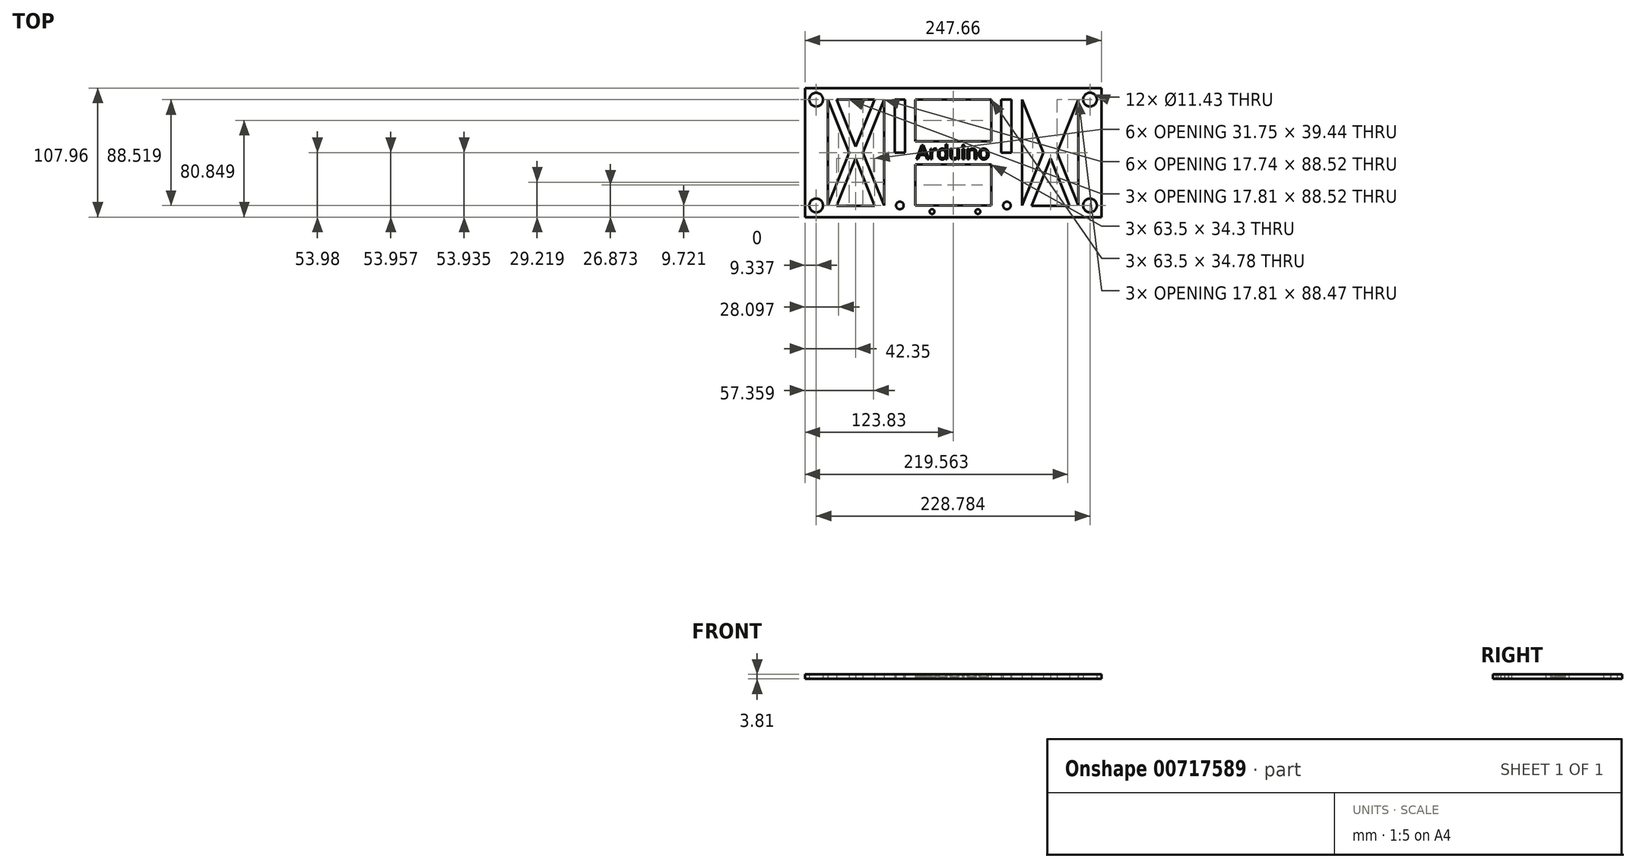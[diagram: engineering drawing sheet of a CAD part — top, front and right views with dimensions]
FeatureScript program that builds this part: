
annotation { "Feature Type Name" : "Feature", "Feature Type Description" : "" }
export const myFeature = defineFeature(function(context is Context, id is Id, definition is map)
    precondition{}
    {
        {
            var Q0;
            Q0=qCreatedBy(makeId("Top.planeOp"),FACE);
            var sketch = newSketch(context, id + "F0", { "sketchPlane" : qUnion([Q0])});
            skLineSegment(sketch, "E0.bottom", {"start": v(-123.83, 53.97) * mm, "end": v(123.83, 53.97) * mm});
            skLineSegment(sketch, "E0.top", {"start": v(-123.83, -53.97) * mm, "end": v(123.83, -53.97) * mm});
            skLineSegment(sketch, "E0.left", {"start": v(-123.83, 53.97) * mm, "end": v(-123.83, -53.97) * mm});
            skLineSegment(sketch, "E0.right", {"start": v(123.83, 53.97) * mm, "end": v(123.83, -53.97) * mm});
            skPoint(sketch, "E0.middle", {"position": v(0, 0) * mm});
            skLineSegment(sketch, "E1.bottom", {"start": v(-31.75, 44.26) * mm, "end": v(31.75, 44.26) * mm});
            skLineSegment(sketch, "E1.top", {"start": v(-31.75, -44.26) * mm, "end": v(31.75, -44.26) * mm});
            skLineSegment(sketch, "E1.left", {"start": v(-31.75, 44.26) * mm, "end": v(-31.75, 9.48) * mm});
            skLineSegment(sketch, "E1.right", {"start": v(31.75, 44.26) * mm, "end": v(31.75, 9.48) * mm});
            skLineSegment(sketch, "E2", {"start": v(-104.64, 44.26) * mm, "end": v(-104.64, -44.26) * mm});
            skLineSegment(sketch, "E3.2.0.0", {"start": v(-57.6, 44.21) * mm, "end": v(-57.6, -44.3) * mm});
            skLineSegment(sketch, "E4", {"start": v(-65.6, 44.21) * mm, "end": v(-97.36, 44.26) * mm});
            skLineSegment(sketch, "E5", {"start": v(-97.36, -44.48) * mm, "end": v(-65.6, -44.48) * mm});
            skLineSegment(sketch, "E6.bottom", {"start": v(-48.82, 44.21) * mm, "end": v(-40.12, 44.21) * mm});
            skLineSegment(sketch, "E6.top", {"start": v(-48.82, 0) * mm, "end": v(-40.12, 0) * mm});
            skLineSegment(sketch, "E6.left", {"start": v(-48.82, 44.21) * mm, "end": v(-48.82, 0) * mm});
            skLineSegment(sketch, "E6.right", {"start": v(-40.12, 44.21) * mm, "end": v(-40.12, 0) * mm});
            skLineSegment(sketch, "E7.1.0.0", {"start": v(97.36, 44.45) * mm, "end": v(65.6, 44.45) * mm});
            skLineSegment(sketch, "E7.1.0.5", {"start": v(65.6, -44.48) * mm, "end": v(97.36, -44.48) * mm});
            skLineSegment(sketch, "E7.1.0.8", {"start": v(104.62, 44.45) * mm, "end": v(104.64, -44.45) * mm});
            skLineSegment(sketch, "E7.1.0.9", {"start": v(57.6, 44.45) * mm, "end": v(57.6, -44.45) * mm});
            skLineSegment(sketch, "E8", {"start": v(0, 0) * mm, "end": v(0, 1.06) * mm, "construction": true});
            skLineSegment(sketch, "E9", {"start": v(0, 6.02) * mm, "end": v(0, 0) * mm, "construction": true});
            skLineSegment(sketch, "E10", {"start": v(0, 0) * mm, "end": v(0, -6.02) * mm, "construction": true});
            skPoint(sketch, "E11.endSnap0", {"position": v(-57.6, -0.04) * mm});
            skLineSegment(sketch, "E12", {"start": v(-75.34, -0.04) * mm, "end": v(-57.6, -44.3) * mm});
            skLineSegment(sketch, "E13", {"start": v(-86.83, 0) * mm, "end": v(-104.64, -44.26) * mm});
            skLineSegment(sketch, "E14", {"start": v(-97.36, -44.48) * mm, "end": v(-81.48, -5.04) * mm});
            skLineSegment(sketch, "E15", {"start": v(-81.48, -5.04) * mm, "end": v(-65.6, -44.48) * mm});
            skLineSegment(sketch, "E16", {"start": v(-57.6, 44.21) * mm, "end": v(-75.34, -0.04) * mm});
            skLineSegment(sketch, "E17", {"start": v(-104.64, 44.26) * mm, "end": v(-86.83, 0) * mm});
            skLineSegment(sketch, "E18", {"start": v(-97.36, 44.26) * mm, "end": v(-81.54, 4.8) * mm});
            skLineSegment(sketch, "E19", {"start": v(-81.54, 4.8) * mm, "end": v(-65.6, 44.21) * mm});
            skLineSegment(sketch, "E20.MirrorCS", {"start": v(81.54, 4.8) * mm, "end": v(65.6, 44.21) * mm});
            skLineSegment(sketch, "E21.MirrorCS", {"start": v(97.36, 44.26) * mm, "end": v(81.54, 4.8) * mm});
            skLineSegment(sketch, "E22.MirrorCS", {"start": v(104.64, 44.26) * mm, "end": v(86.83, 0) * mm});
            skLineSegment(sketch, "E23.MirrorCS", {"start": v(57.6, 44.21) * mm, "end": v(75.34, -0.04) * mm});
            skLineSegment(sketch, "E24.MirrorCS", {"start": v(75.34, -0.04) * mm, "end": v(57.6, -44.3) * mm});
            skLineSegment(sketch, "E25.MirrorCS", {"start": v(81.48, -5.04) * mm, "end": v(65.6, -44.48) * mm});
            skLineSegment(sketch, "E26.MirrorCS", {"start": v(97.36, -44.48) * mm, "end": v(81.48, -5.04) * mm});
            skLineSegment(sketch, "E27.MirrorCS", {"start": v(86.83, 0) * mm, "end": v(104.64, -44.26) * mm});
            skLineSegment(sketch, "E28", {"start": v(-31.75, 9.48) * mm, "end": v(31.75, 9.48) * mm});
            skLineSegment(sketch, "E29", {"start": v(-31.75, -9.95) * mm, "end": v(31.75, -9.95) * mm});
            skLineSegment(sketch, "E30.trimOffspring", {"start": v(-31.75, -9.95) * mm, "end": v(-31.75, -44.26) * mm});
            skLineSegment(sketch, "E31.trimOffspring", {"start": v(31.75, -9.95) * mm, "end": v(31.75, -44.26) * mm});
            skCircle(sketch, "E32", {"center": v(-114.5, -44.26) * mm, "radius": 5.72 * mm});
            skCircle(sketch, "E33", {"center": v(-114.5, 44.26) * mm, "radius": 5.72 * mm});
            skCircle(sketch, "E34", {"center": v(114.3, 44.26) * mm, "radius": 5.72 * mm});
            skCircle(sketch, "E35", {"center": v(114.3, -44.26) * mm, "radius": 5.72 * mm});
            skLineSegment(sketch, "E36", {"start": v(40.03, 44.26) * mm, "end": v(40.03, 0) * mm});
            skLineSegment(sketch, "E37", {"start": v(40.03, 0) * mm, "end": v(48.72, 0) * mm});
            skLineSegment(sketch, "E38", {"start": v(48.72, 0) * mm, "end": v(48.72, 44.45) * mm});
            skLineSegment(sketch, "E39", {"start": v(48.72, 44.45) * mm, "end": v(40.03, 44.26) * mm});
            skCircle(sketch, "E40", {"center": v(-44.53, -44.26) * mm, "radius": 3.18 * mm});
            skCircle(sketch, "E41", {"center": v(44.87, -44.3) * mm, "radius": 3.18 * mm});
            skCircle(sketch, "E42", {"center": v(-17.66, -49.42) * mm, "radius": 2.03 * mm});
            skCircle(sketch, "E43", {"center": v(20.65, -49.42) * mm, "radius": 2.03 * mm});
            skSolve(sketch);
        }
        {
            var Q0;
            Q0=makeQuery(id+"F0.imprint","IMPRINT",FACE,{"disambiguationData":[TD([[makeQuery(id+"F0.imprint","IMPRINT",EDGE,{"derivedFrom":sQuery(id+"F0.wireOp",EDGE,"E0.bottom")}),-1.0]])]});
            extrude(context, id + "F1", {"entities" : qUnion([Q0]), "depth" : 3.8 * mm, "offsetDistance" : 25.4 * mm});
        }
        {
            var Q0;
            Q0=makeQuery(id+"F1.opExtrude","CAP_FACE",FACE,{"disambiguationData":[OSD([sQuery(id+"F0.wireOp",EDGE,"E0.bottom"),sQuery(id+"F0.wireOp",EDGE,"E0.top"),sQuery(id+"F0.wireOp",EDGE,"E0.left"),sQuery(id+"F0.wireOp",EDGE,"E0.right"),sQuery(id+"F0.wireOp",EDGE,"E1.bottom"),sQuery(id+"F0.wireOp",EDGE,"E1.top"),sQuery(id+"F0.wireOp",EDGE,"E1.left"),sQuery(id+"F0.wireOp",EDGE,"E1.right"),sQuery(id+"F0.wireOp",EDGE,"E2"),sQuery(id+"F0.wireOp",EDGE,"E3.2.0.0"),sQuery(id+"F0.wireOp",EDGE,"E4"),sQuery(id+"F0.wireOp",EDGE,"E5"),sQuery(id+"F0.wireOp",EDGE,"E6.bottom"),sQuery(id+"F0.wireOp",EDGE,"E6.top"),sQuery(id+"F0.wireOp",EDGE,"E6.left"),sQuery(id+"F0.wireOp",EDGE,"E6.right"),sQuery(id+"F0.wireOp",EDGE,"EDbcc8To-gHE8-0e38-XdKg-VJ03WfKCGKzv.top"),sQuery(id+"F0.wireOp",EDGE,"PwnecxsJ-G9VO-R5J2-sHQL-yZhxZq1WzkO5.top"),sQuery(id+"F0.wireOp",EDGE,"knHNyI9P-ag72-iEyU-8EV8-doZ3lSehcMvr.right"),sQuery(id+"F0.wireOp",EDGE,"xFymK1IS-Nx3j-6yMD-4VB3-YUyhBz9Zr5L7.right"),sQuery(id+"F0.wireOp",EDGE,"E7.1.0.0"),sQuery(id+"F0.wireOp",EDGE,"E7.1.0.5"),sQuery(id+"F0.wireOp",EDGE,"E7.1.0.8"),sQuery(id+"F0.wireOp",EDGE,"E7.1.0.9"),sQuery(id+"F0.wireOp",EDGE,"207002f3-aa39-43c8-9de0-26d269d94b6c.1.0.0"),sQuery(id+"F0.wireOp",EDGE,"207002f3-aa39-43c8-9de0-26d269d94b6c.1.0.1"),sQuery(id+"F0.wireOp",EDGE,"207002f3-aa39-43c8-9de0-26d269d94b6c.1.0.2"),sQuery(id+"F0.wireOp",EDGE,"207002f3-aa39-43c8-9de0-26d269d94b6c.1.0.3"),sQuery(id+"F0.wireOp",EDGE,"207002f3-aa39-43c8-9de0-26d269d94b6c.1.0.4"),sQuery(id+"F0.wireOp",EDGE,"207002f3-aa39-43c8-9de0-26d269d94b6c.1.0.5"),sQuery(id+"F0.wireOp",EDGE,"207002f3-aa39-43c8-9de0-26d269d94b6c.1.0.6"),sQuery(id+"F0.wireOp",EDGE,"207002f3-aa39-43c8-9de0-26d269d94b6c.1.0.7"),sQuery(id+"F0.wireOp",EDGE,"E12"),sQuery(id+"F0.wireOp",EDGE,"E13"),sQuery(id+"F0.wireOp",EDGE,"E14"),sQuery(id+"F0.wireOp",EDGE,"E15"),sQuery(id+"F0.wireOp",EDGE,"E16"),sQuery(id+"F0.wireOp",EDGE,"E17"),sQuery(id+"F0.wireOp",EDGE,"E18"),sQuery(id+"F0.wireOp",EDGE,"E19"),sQuery(id+"F0.wireOp",EDGE,"E20.MirrorCS"),sQuery(id+"F0.wireOp",EDGE,"E21.MirrorCS"),sQuery(id+"F0.wireOp",EDGE,"E22.MirrorCS"),sQuery(id+"F0.wireOp",EDGE,"E23.MirrorCS"),sQuery(id+"F0.wireOp",EDGE,"E24.MirrorCS"),sQuery(id+"F0.wireOp",EDGE,"E25.MirrorCS"),sQuery(id+"F0.wireOp",EDGE,"E26.MirrorCS"),sQuery(id+"F0.wireOp",EDGE,"E27.MirrorCS"),sQuery(id+"F0.wireOp",EDGE,"E28"),sQuery(id+"F0.wireOp",EDGE,"E29"),sQuery(id+"F0.wireOp",EDGE,"E30.trimOffspring"),sQuery(id+"F0.wireOp",EDGE,"E31.trimOffspring")])],"isStart":false});
            var sketch = newSketch(context, id + "F2", { "sketchPlane" : qUnion([Q0])});
            skText(sketch, "E44", { "text": "Arduino", "fontName": "OpenSans-Regular.ttf"});
            const initialGuessF2  = {"E44": [-0.03075, -0.00564, 1, 0, 0.0118]};
            skSetInitialGuess(sketch, initialGuessF2);
            skSolve(sketch);
        }
        {
            var Q0;
            Q0=qSketchRegion(id+"F2",true);
            extrude(context, id + "F3", {"entities" : qUnion([Q0]), "operationType" : NewBodyOperationType.REMOVE, "oppositeDirection" : true, "depth" : 2.03 * mm, "offsetDistance" : 25.4 * mm});
        }
    });
